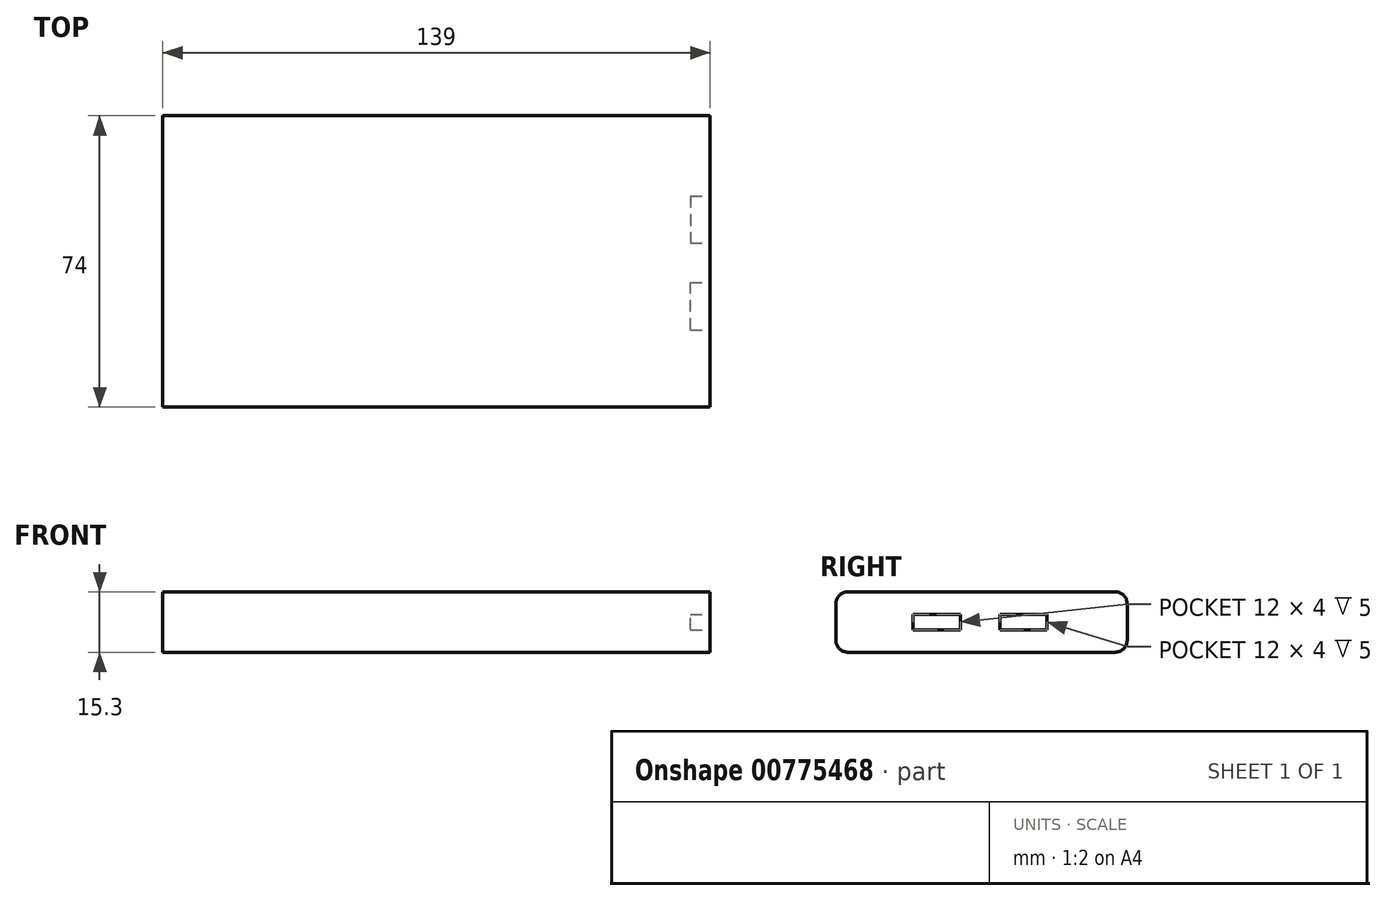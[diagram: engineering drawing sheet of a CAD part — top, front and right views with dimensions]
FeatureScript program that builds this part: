
annotation { "Feature Type Name" : "Feature", "Feature Type Description" : "" }
export const myFeature = defineFeature(function(context is Context, id is Id, definition is map)
    precondition{}
    {
        {
            var Q0;
            Q0=qCreatedBy(makeId("Right.planeOp"),FACE);
            var sketch = newSketch(context, id + "F0", { "sketchPlane" : qUnion([Q0])});
            skLineSegment(sketch, "E0.bottom", {"start": v(-37, 7.65) * mm, "end": v(37, 7.65) * mm});
            skLineSegment(sketch, "E0.top", {"start": v(-37, -7.65) * mm, "end": v(37, -7.65) * mm});
            skLineSegment(sketch, "E0.left", {"start": v(-37, 7.65) * mm, "end": v(-37, -7.65) * mm});
            skLineSegment(sketch, "E0.right", {"start": v(37, 7.65) * mm, "end": v(37, -7.65) * mm});
            skPoint(sketch, "E0.middle", {"position": v(0, 0) * mm});
            skSolve(sketch);
        }
        {
            var Q0;
            Q0=makeQuery(id+"F0.imprint","IMPRINT",FACE,{"disambiguationData":[TD([[makeQuery(id+"F0.imprint","IMPRINT",EDGE,{"derivedFrom":sQuery(id+"F0.wireOp",EDGE,"E0.bottom")}),-1.0]])]});
            extrude(context, id + "F1", {"entities" : qUnion([Q0]), "endBound" : BoundingType.SYMMETRIC, "depth" : 139 * mm, "offsetDistance" : 25 * mm});
        }
        {
            var Q0;
            Q0=makeQuery(id+"F1.opExtrude","SWEPT_EDGE",EDGE,{"disambiguationData":[OSD([sQuery(id+"F0.wireOp",EDGE,"E0.bottom"),sQuery(id+"F0.wireOp",EDGE,"E0.left")])]});
            var Q1;
            Q1=makeQuery(id+"F1.opExtrude","SWEPT_EDGE",EDGE,{"disambiguationData":[OSD([sQuery(id+"F0.wireOp",EDGE,"E0.bottom"),sQuery(id+"F0.wireOp",EDGE,"E0.right")])]});
            var Q2;
            Q2=makeQuery(id+"F1.opExtrude","SWEPT_EDGE",EDGE,{"disambiguationData":[OSD([sQuery(id+"F0.wireOp",EDGE,"E0.top"),sQuery(id+"F0.wireOp",EDGE,"E0.right")])]});
            var Q3;
            Q3=makeQuery(id+"F1.opExtrude","SWEPT_EDGE",EDGE,{"disambiguationData":[OSD([sQuery(id+"F0.wireOp",EDGE,"E0.top"),sQuery(id+"F0.wireOp",EDGE,"E0.left")])]});
            fillet(context, id + "F2", {"entities" : qUnion([Q0, Q1, Q2, Q3]), "radius" : 3 * mm, "tangentPropagation" : true, "allowEdgeOverflow" : false});
        }
        {
            var Q0;
            Q0=makeQuery(id+"F1.opExtrude","CAP_FACE",FACE,{"disambiguationData":[OSD([sQuery(id+"F0.wireOp",EDGE,"E0.bottom"),sQuery(id+"F0.wireOp",EDGE,"E0.top"),sQuery(id+"F0.wireOp",EDGE,"E0.left"),sQuery(id+"F0.wireOp",EDGE,"E0.right")])],"isStart":false});
            var sketch = newSketch(context, id + "F3", { "sketchPlane" : qUnion([Q0])});
            skLineSegment(sketch, "E1.bottom", {"start": v(16.61, -2) * mm, "end": v(4.61, -2) * mm});
            skLineSegment(sketch, "E1.top", {"start": v(16.61, 2) * mm, "end": v(4.61, 2) * mm});
            skLineSegment(sketch, "E1.left", {"start": v(16.61, -2) * mm, "end": v(16.61, 2) * mm});
            skLineSegment(sketch, "E1.right", {"start": v(4.61, -2) * mm, "end": v(4.61, 2) * mm});
            skPoint(sketch, "E1.middle", {"position": v(10.61, 0) * mm});
            skLineSegment(sketch, "E2.bottom", {"start": v(-17.39, -2) * mm, "end": v(-5.39, -2) * mm});
            skLineSegment(sketch, "E2.top", {"start": v(-17.39, 2) * mm, "end": v(-5.39, 2) * mm});
            skLineSegment(sketch, "E2.left", {"start": v(-17.39, -2) * mm, "end": v(-17.39, 2) * mm});
            skLineSegment(sketch, "E2.right", {"start": v(-5.39, -2) * mm, "end": v(-5.39, 2) * mm});
            skPoint(sketch, "E2.middle", {"position": v(-11.39, 0) * mm});
            skSolve(sketch);
        }
        {
            var Q0;
            Q0=makeQuery(id+"F3.imprint","IMPRINT",FACE,{"disambiguationData":[TD([[makeQuery(id+"F3.imprint","IMPRINT",EDGE,{"derivedFrom":sQuery(id+"F3.wireOp",EDGE,"E1.bottom")}),-1.0]])]});
            var Q1;
            Q1=makeQuery(id+"F3.imprint","IMPRINT",FACE,{"disambiguationData":[TD([[makeQuery(id+"F3.imprint","IMPRINT",EDGE,{"derivedFrom":sQuery(id+"F3.wireOp",EDGE,"E2.bottom")}),1.0]])]});
            extrude(context, id + "F4", {"entities" : qUnion([Q0, Q1]), "operationType" : NewBodyOperationType.REMOVE, "oppositeDirection" : true, "depth" : 5 * mm, "offsetDistance" : 25 * mm});
        }
    });
